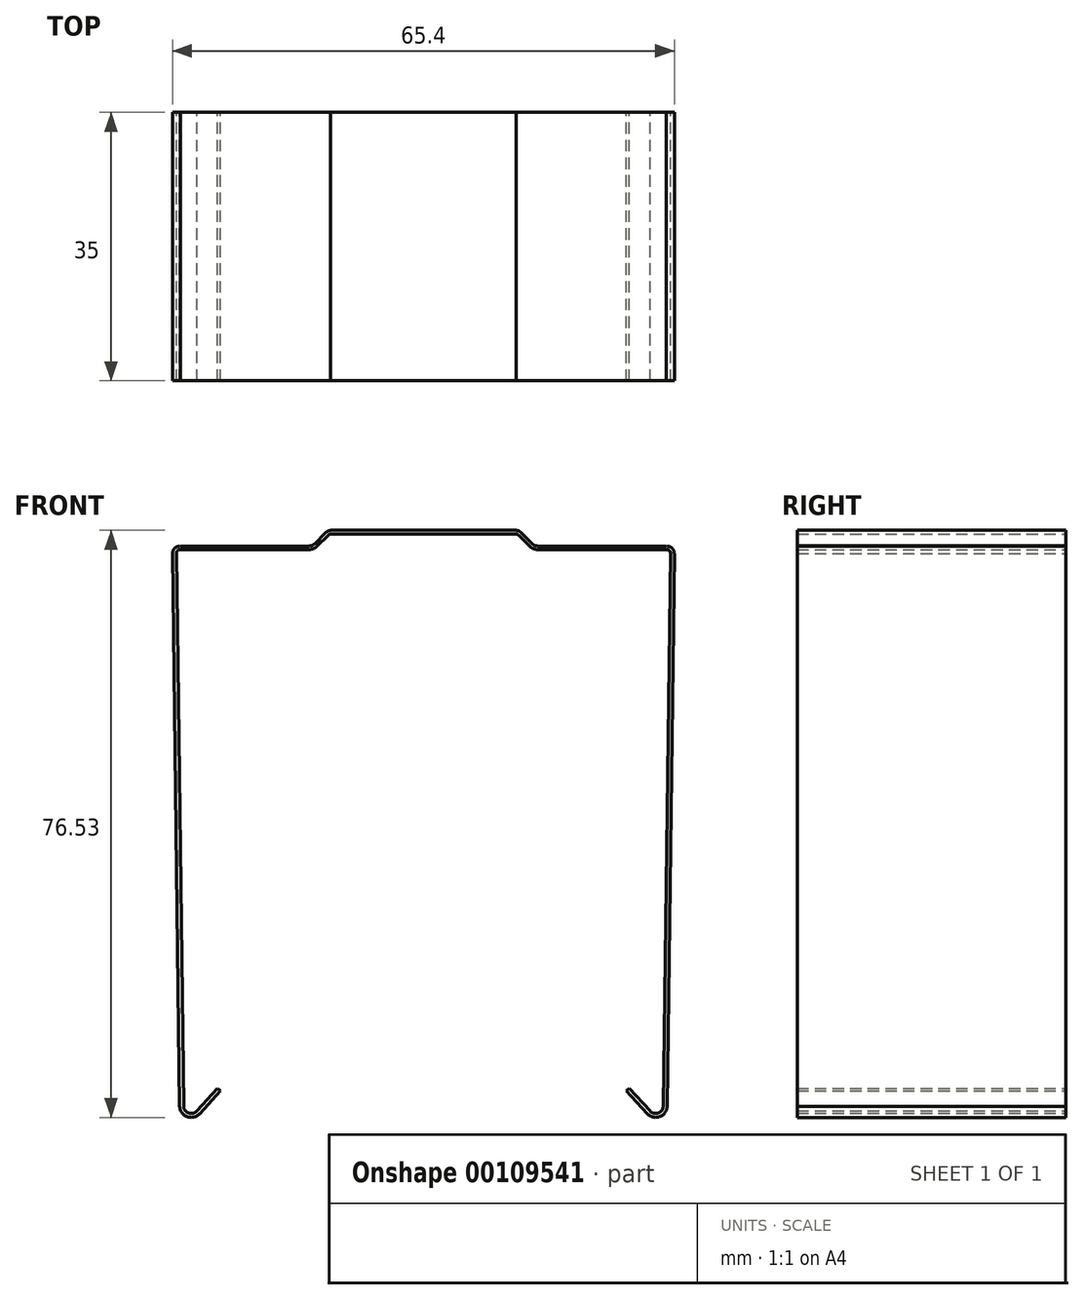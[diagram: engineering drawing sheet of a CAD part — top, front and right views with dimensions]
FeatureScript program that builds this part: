
annotation { "Feature Type Name" : "Feature", "Feature Type Description" : "" }
export const myFeature = defineFeature(function(context is Context, id is Id, definition is map)
    precondition{}
    {
        {
            var Q0;
            Q0=qCreatedBy(makeId("Front.planeOp"),FACE);
            var sketch = newSketch(context, id + "F0", { "sketchPlane" : qUnion([Q0])});
            skLineSegment(sketch, "E0", {"start": v(0, 0) * mm, "end": v(12.09, 0) * mm});
            skLineSegment(sketch, "E1", {"start": v(14.17, -1.74) * mm, "end": v(12.71, -0.29) * mm});
            skArc(sketch, "E2", {"start": v(12.71, -0.29) * mm, "mid": v(12.43, -0.09) * mm, "end": v(12.09, 0) * mm});
            skLineSegment(sketch, "E3", {"start": v(14.88, -2.04) * mm, "end": v(31.66, -2.04) * mm});
            skLineSegment(sketch, "E4", {"start": v(32.7, -3.05) * mm, "end": v(31.76, -75.1) * mm});
            skArc(sketch, "E5", {"start": v(32.7, -3.05) * mm, "mid": v(32.4, -2.32) * mm, "end": v(31.66, -2.04) * mm});
            skLineSegment(sketch, "E6", {"start": v(26.47, -73.06) * mm, "end": v(29.15, -76.03) * mm});
            skArc(sketch, "E7", {"start": v(29.15, -76.03) * mm, "mid": v(30.77, -76.44) * mm, "end": v(31.76, -75.1) * mm});
            skLineSegment(sketch, "E8", {"start": v(26.47, -73.06) * mm, "end": v(26.84, -72.73) * mm});
            skLineSegment(sketch, "E9", {"start": v(26.84, -72.73) * mm, "end": v(29.52, -75.7) * mm});
            skLineSegment(sketch, "E10", {"start": v(31.25, -75.03) * mm, "end": v(32.2, -3.03) * mm});
            skArc(sketch, "E11", {"start": v(29.52, -75.7) * mm, "mid": v(30.61, -75.94) * mm, "end": v(31.25, -75.03) * mm});
            skLineSegment(sketch, "E12", {"start": v(14.91, -2.5) * mm, "end": v(31.7, -2.5) * mm});
            skArc(sketch, "E13", {"start": v(32.2, -3.03) * mm, "mid": v(32.06, -2.66) * mm, "end": v(31.7, -2.5) * mm});
            skArc(sketch, "E14", {"start": v(14.17, -1.74) * mm, "mid": v(14.5, -1.96) * mm, "end": v(14.88, -2.04) * mm});
            skLineSegment(sketch, "E15", {"start": v(12.44, -0.65) * mm, "end": v(13.85, -2.06) * mm});
            skArc(sketch, "E16", {"start": v(13.85, -2.06) * mm, "mid": v(14.34, -2.39) * mm, "end": v(14.91, -2.5) * mm});
            skLineSegment(sketch, "E17", {"start": v(0, 0) * mm, "end": v(0, -0.5) * mm});
            skLineSegment(sketch, "E18", {"start": v(12.09, -0.5) * mm, "end": v(0, -0.5) * mm});
            skArc(sketch, "E19", {"start": v(12.44, -0.65) * mm, "mid": v(12.28, -0.54) * mm, "end": v(12.09, -0.5) * mm});
            skArc(sketch, "E20.MirrorCS", {"start": v(-12.71, -0.29) * mm, "mid": v(-12.43, -0.09) * mm, "end": v(-12.09, 0) * mm});
            skArc(sketch, "E21.MirrorCS", {"start": v(-14.17, -1.74) * mm, "mid": v(-14.5, -1.96) * mm, "end": v(-14.88, -2.04) * mm});
            skArc(sketch, "E22.MirrorCS", {"start": v(-12.44, -0.65) * mm, "mid": v(-12.28, -0.54) * mm, "end": v(-12.09, -0.5) * mm});
            skArc(sketch, "E23.MirrorCS", {"start": v(-13.85, -2.06) * mm, "mid": v(-14.34, -2.39) * mm, "end": v(-14.91, -2.5) * mm});
            skLineSegment(sketch, "E24.MirrorCS", {"start": v(-26.47, -73.06) * mm, "end": v(-26.84, -72.73) * mm});
            skArc(sketch, "E25.MirrorCS", {"start": v(-32.2, -3.03) * mm, "mid": v(-32.06, -2.66) * mm, "end": v(-31.7, -2.5) * mm});
            skArc(sketch, "E26.MirrorCS", {"start": v(-29.52, -75.7) * mm, "mid": v(-30.61, -75.94) * mm, "end": v(-31.25, -75.03) * mm});
            skArc(sketch, "E27.MirrorCS", {"start": v(-32.7, -3.05) * mm, "mid": v(-32.4, -2.32) * mm, "end": v(-31.66, -2.04) * mm});
            skLineSegment(sketch, "E28.MirrorCS", {"start": v(-14.17, -1.74) * mm, "end": v(-12.71, -0.29) * mm});
            skLineSegment(sketch, "E29.MirrorCS", {"start": v(-12.44, -0.65) * mm, "end": v(-13.85, -2.06) * mm});
            skLineSegment(sketch, "E30.MirrorCS", {"start": v(-12.09, -0.5) * mm, "end": v(0, -0.5) * mm});
            skLineSegment(sketch, "E31.MirrorCS", {"start": v(-14.91, -2.5) * mm, "end": v(-31.7, -2.5) * mm});
            skLineSegment(sketch, "E32.MirrorCS", {"start": v(-31.25, -75.03) * mm, "end": v(-32.2, -3.03) * mm});
            skLineSegment(sketch, "E33.MirrorCS", {"start": v(-26.84, -72.73) * mm, "end": v(-29.52, -75.7) * mm});
            skArc(sketch, "E34.MirrorCS", {"start": v(-29.15, -76.03) * mm, "mid": v(-30.77, -76.44) * mm, "end": v(-31.76, -75.1) * mm});
            skLineSegment(sketch, "E35.MirrorCS", {"start": v(-26.47, -73.06) * mm, "end": v(-29.15, -76.03) * mm});
            skLineSegment(sketch, "E36.MirrorCS", {"start": v(-32.7, -3.05) * mm, "end": v(-31.76, -75.1) * mm});
            skLineSegment(sketch, "E37.MirrorCS", {"start": v(0, 0) * mm, "end": v(-12.09, 0) * mm});
            skLineSegment(sketch, "E38.MirrorCS", {"start": v(-14.88, -2.04) * mm, "end": v(-31.66, -2.04) * mm});
            skLineSegment(sketch, "E39", {"start": v(32.2, -3.03) * mm, "end": v(40.94, -3.03) * mm, "construction": true});
            skLineSegment(sketch, "E40", {"start": v(31.25, -75.03) * mm, "end": v(43.25, -75.03) * mm, "construction": true});
            skSolve(sketch);
        }
        {
            var Q0;
            Q0 = qSketchRegion(id + "F0", true);
            extrude(context, id + "F1", {"entities" : qUnion([Q0]), "depth" : 35 * mm});
        }
    });
